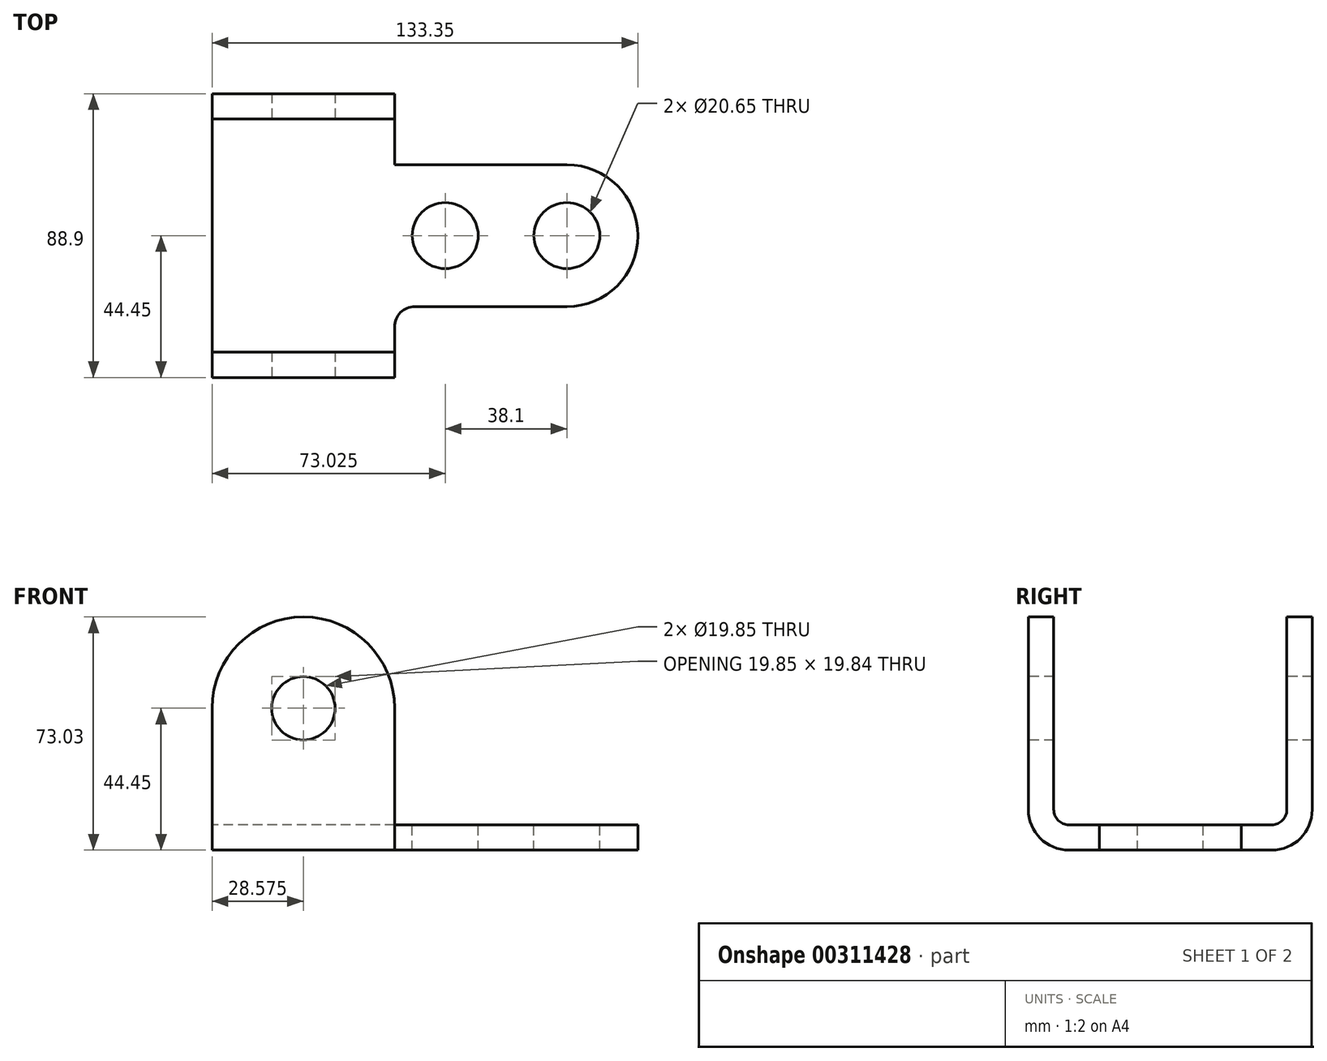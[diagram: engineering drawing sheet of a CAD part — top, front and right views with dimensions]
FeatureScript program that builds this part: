
annotation { "Feature Type Name" : "Feature", "Feature Type Description" : "" }
export const myFeature = defineFeature(function(context is Context, id is Id, definition is map)
    precondition{}
    {
        {
            var Q0;
            Q0=qCreatedBy(makeId("Right.planeOp"),FACE);
            var sketch = newSketch(context, id + "F0", { "sketchPlane" : qUnion([Q0])});
            skLineSegment(sketch, "E0.bottom", {"start": v(0, 0) * mm, "end": v(88.9, 0) * mm});
            skLineSegment(sketch, "E0.top", {"start": v(0, 44.45) * mm, "end": v(7.94, 44.45) * mm});
            skLineSegment(sketch, "E0.left", {"start": v(0, 0) * mm, "end": v(0, 44.45) * mm});
            skLineSegment(sketch, "E0.right", {"start": v(88.9, 0) * mm, "end": v(88.9, 44.45) * mm});
            skLineSegment(sketch, "E1.top", {"start": v(7.94, 7.94) * mm, "end": v(80.96, 7.94) * mm});
            skLineSegment(sketch, "E1.left", {"start": v(7.94, 44.45) * mm, "end": v(7.94, 7.94) * mm});
            skLineSegment(sketch, "E1.right", {"start": v(80.96, 44.45) * mm, "end": v(80.96, 7.94) * mm});
            skLineSegment(sketch, "E2.trimOffspring", {"start": v(80.96, 44.45) * mm, "end": v(88.9, 44.45) * mm});
            skSolve(sketch);
        }
        {
            var Q0;
            Q0 = qSketchRegion(id + "F0", true);
            extrude(context, id + "F1", {"entities" : qUnion([Q0]), "depth" : 57.15 * mm});
        }
        {
            var Q0;
            Q0=makeQuery(id+"F1.opExtrude","SWEPT_FACE",FACE,{"disambiguationData":[OSD([sQuery(id+"F0.wireOp",EDGE,"E0.left")])]});
            var sketch = newSketch(context, id + "F2", { "sketchPlane" : qUnion([Q0])});
            skArc(sketch, "E3", {"start": v(57.15, 44.45) * mm, "mid": v(28.58, 73.03) * mm, "end": v(0, 44.45) * mm});
            skLineSegment(sketch, "E4", {"start": v(0, 44.45) * mm, "end": v(57.15, 44.45) * mm});
            skSolve(sketch);
        }
        {
            var Q0;
            Q0 = qSketchRegion(id + "F2", true);
            extrude(context, id + "F3", {"entities" : qUnion([Q0]), "operationType" : NewBodyOperationType.ADD, "oppositeDirection" : true, "depth" : 7.94 * mm});
        }
        {
            var Q0;
            Q0=makeQuery(id+"F1.opExtrude","SWEPT_FACE",FACE,{"disambiguationData":[OSD([sQuery(id+"F0.wireOp",EDGE,"E0.right")])]});
            var sketch = newSketch(context, id + "F4", { "sketchPlane" : qUnion([Q0])});
            skArc(sketch, "E5", {"start": v(0, 44.45) * mm, "mid": v(-28.58, 73.02) * mm, "end": v(-57.15, 44.45) * mm});
            skLineSegment(sketch, "E6", {"start": v(-57.15, 44.45) * mm, "end": v(0, 44.45) * mm});
            skSolve(sketch);
        }
        {
            var Q0;
            Q0 = qSketchRegion(id + "F4", true);
            extrude(context, id + "F5", {"entities" : qUnion([Q0]), "operationType" : NewBodyOperationType.ADD, "oppositeDirection" : true, "depth" : 7.94 * mm});
        }
        {
            var Q0;
            Q0=makeQuery(id+"F3.boolean.opBoolean","MERGE",FACE,{"derivedFrom":[makeQuery(id+"F1.opExtrude","SWEPT_FACE",FACE,{"disambiguationData":[OSD([sQuery(id+"F0.wireOp",EDGE,"E0.left")])]}),makeQuery(id+"F3.opExtrude","CAP_FACE",FACE,{"disambiguationData":[OSD([sQuery(id+"F2.wireOp",EDGE,"E3"),sQuery(id+"F2.wireOp",EDGE,"E4")])],"isStart":true})]});
            var sketch = newSketch(context, id + "F6", { "sketchPlane" : qUnion([Q0])});
            skCircle(sketch, "E7", {"center": v(28.58, 44.45) * mm, "radius": 9.92 * mm});
            skSolve(sketch);
        }
        {
            var Q0;
            Q0 = qSketchRegion(id + "F6", true);
            extrude(context, id + "F7", {"entities" : qUnion([Q0]), "operationType" : NewBodyOperationType.REMOVE, "endBound" : BoundingType.THROUGH_ALL, "oppositeDirection" : true, "depth" : 25.4 * mm});
        }
        {
            var Q0;
            Q0=makeQuery(id+"F1.opExtrude","SWEPT_FACE",FACE,{"disambiguationData":[OSD([sQuery(id+"F0.wireOp",EDGE,"E1.top")])]});
            var sketch = newSketch(context, id + "F8", { "sketchPlane" : qUnion([Q0])});
            skLineSegment(sketch, "E8.bottom", {"start": v(57.15, 22.23) * mm, "end": v(111.12, 22.23) * mm});
            skLineSegment(sketch, "E8.top", {"start": v(57.15, 66.67) * mm, "end": v(111.12, 66.67) * mm});
            skLineSegment(sketch, "E8.left", {"start": v(57.15, 22.23) * mm, "end": v(57.15, 66.67) * mm});
            skLineSegment(sketch, "E8.right", {"start": v(111.12, 22.23) * mm, "end": v(111.12, 66.67) * mm});
            skArc(sketch, "E9", {"start": v(111.12, 22.22) * mm, "mid": v(133.35, 44.45) * mm, "end": v(111.12, 66.67) * mm});
            skSolve(sketch);
        }
        {
            var Q0;
            Q0 = qSketchRegion(id + "F8", true);
            extrude(context, id + "F9", {"entities" : qUnion([Q0]), "operationType" : NewBodyOperationType.ADD, "oppositeDirection" : true, "depth" : 7.94 * mm});
        }
        {
            var Q0;
            Q0=makeQuery(id+"F9.boolean.opBoolean","MERGE",FACE,{"derivedFrom":[makeQuery(id+"F1.opExtrude","SWEPT_FACE",FACE,{"disambiguationData":[OSD([sQuery(id+"F0.wireOp",EDGE,"E1.top")])]}),makeQuery(id+"F9.opExtrude","CAP_FACE",FACE,{"disambiguationData":[OSD([sQuery(id+"F8.wireOp",EDGE,"E8.bottom"),sQuery(id+"F8.wireOp",EDGE,"E8.top"),sQuery(id+"F8.wireOp",EDGE,"E8.left"),sQuery(id+"F8.wireOp",EDGE,"E9")])],"isStart":true})]});
            var sketch = newSketch(context, id + "F10", { "sketchPlane" : qUnion([Q0])});
            skCircle(sketch, "E10", {"center": v(73.03, 44.45) * mm, "radius": 10.33 * mm});
            skPoint(sketch, "E10.centerSnap0", {"position": v(133.35, 44.45) * mm});
            skCircle(sketch, "E11", {"center": v(111.12, 44.45) * mm, "radius": 10.33 * mm});
            skSolve(sketch);
        }
        {
            var Q0;
            Q0 = qSketchRegion(id + "F10", true);
            extrude(context, id + "F11", {"entities" : qUnion([Q0]), "operationType" : NewBodyOperationType.REMOVE, "endBound" : BoundingType.THROUGH_ALL, "oppositeDirection" : true, "depth" : 25.4 * mm});
        }
        {
            var Q0;
            Q0=makeQuery(id+"F1.opExtrude","SWEPT_EDGE",EDGE,{"disambiguationData":[OSD([sQuery(id+"F0.wireOp",EDGE,"E1.top"),sQuery(id+"F0.wireOp",EDGE,"E1.right")])]});
            var Q1;
            Q1=makeQuery(id+"F1.opExtrude","SWEPT_EDGE",EDGE,{"disambiguationData":[OSD([sQuery(id+"F0.wireOp",EDGE,"E1.top"),sQuery(id+"F0.wireOp",EDGE,"E1.left")])]});
            fillet(context, id + "F12", {"entities" : qUnion([Q0, Q1]), "radius" : 4.76 * mm, "tangentPropagation" : true, "allowEdgeOverflow" : false});
        }
        {
            var Q0;
            Q0=makeQuery(id+"F1.opExtrude","SWEPT_EDGE",EDGE,{"disambiguationData":[OSD([sQuery(id+"F0.wireOp",EDGE,"E0.bottom"),sQuery(id+"F0.wireOp",EDGE,"E0.left")])]});
            var Q1;
            Q1=makeQuery(id+"F1.opExtrude","SWEPT_EDGE",EDGE,{"disambiguationData":[OSD([sQuery(id+"F0.wireOp",EDGE,"E0.bottom"),sQuery(id+"F0.wireOp",EDGE,"E0.right")])]});
            fillet(context, id + "F13", {"entities" : qUnion([Q0, Q1]), "radius" : 12.7 * mm, "tangentPropagation" : true, "allowEdgeOverflow" : false});
        }
        {
            var Q0;
            Q0=makeQuery(id+"F9.opExtrude","SWEPT_EDGE",EDGE,{"disambiguationData":[OSD([sQuery(id+"F0.wireOp",EDGE,"E1.top"),sQuery(id+"F8.wireOp",EDGE,"E8.top"),sQuery(id+"F8.wireOp",EDGE,"E8.left")])]});
            var Q1;
            Q1=makeQuery(id+"F9.opExtrude","SWEPT_EDGE",EDGE,{"disambiguationData":[OSD([sQuery(id+"F0.wireOp",EDGE,"E1.top"),sQuery(id+"F8.wireOp",EDGE,"E8.bottom"),sQuery(id+"F8.wireOp",EDGE,"E8.left")])]});
            fillet(context, id + "F14", {"entities" : qUnion([Q0, Q1]), "radius" : 6.35 * mm, "tangentPropagation" : true, "allowEdgeOverflow" : false});
        }
    });
